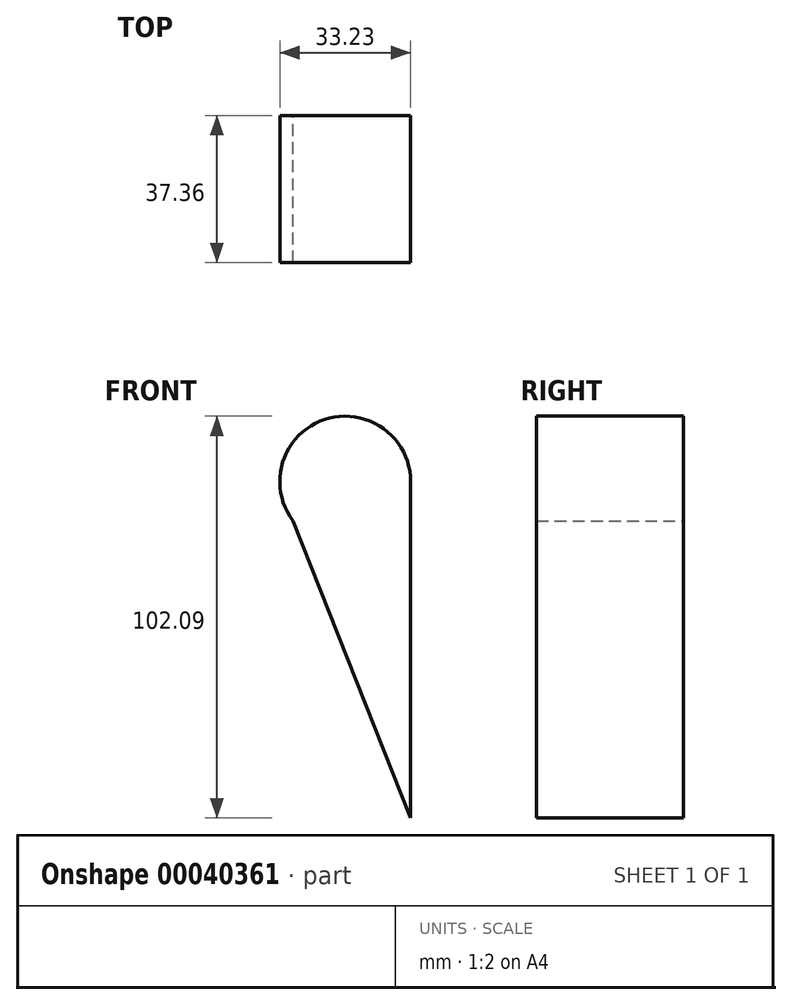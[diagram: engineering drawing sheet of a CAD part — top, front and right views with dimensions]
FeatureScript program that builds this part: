
annotation { "Feature Type Name" : "Feature", "Feature Type Description" : "" }
export const myFeature = defineFeature(function(context is Context, id is Id, definition is map)
    precondition{}
    {
        {
            var Q0;
            Q0=qCreatedBy(makeId("Front.planeOp"),FACE);
            var sketch = newSketch(context, id + "F0", { "sketchPlane" : qUnion([Q0])});
            skCircle(sketch, "E0", {"center": v(-64.98, 45.98) * mm, "radius": 16.61 * mm});
            skLineSegment(sketch, "E1", {"start": v(-48.37, 46.02) * mm, "end": v(-48.37, -39.5) * mm});
            skLineSegment(sketch, "E2", {"start": v(-81.5, 44.15) * mm, "end": v(-48.37, -39.5) * mm});
            skSolve(sketch);
        }
        {
            var Q0;
            Q0 = qSketchRegion(id + "F0", true);
            extrude(context, id + "F1", {"entities" : qUnion([Q0]), "depth" : 37.36 * mm});
        }
    });
